FCSTD DOCUMENT  (FreeCAD 1.0R39109 (Git))
Label: Self Tap screw sketches V2
License: All rights reserved
LicenseURL: https://en.wikipedia.org/wiki/All_rights_reserved
objects: Sketcher::SketchObject×3
note: 6 computed .brp shape members not serialized (recipe doc carries the construction recipe); baked Part::Feature solids carry a one-line shape summary decoded from their .brp

FEATURE [Sketcher::SketchObject] Sketch  label="M3 self tap Sketch"
  ArcFitTolerance = 1e-06
  FullyConstrained = false
  MakeInternals = false
  MapMode = 5
  expr: Constraints[19] = .Constraints.Holeradius * 2 + 0.9 mm
  expr: Constraints[22] = .Constraints.Holeradius / 2
  sketch-geometry (10):
    g0: ArcOfCircle CenterX=-0.517439 CenterY=0.767765 CenterZ=0 NormalX=0 NormalY=0 NormalZ=1 AngleXU=0 Radius=1.6 StartAngle=0.890878 EndAngle=2.25072
    g1: ArcOfCircle CenterX=1.25791 CenterY=1.79277 CenterZ=0 NormalX=0 NormalY=0 NormalZ=1 AngleXU=0 Radius=0.8 StartAngle=2.86405 EndAngle=4.46634
    g2: ArcOfCircle CenterX=-0.517439 CenterY=0.767765 CenterZ=0 NormalX=0 NormalY=0 NormalZ=1 AngleXU=0 Radius=1.6 StartAngle=5.07967 EndAngle=6.43951
    g3: ArcOfCircle CenterX=-0.517439 CenterY=-1.28224 CenterZ=0 NormalX=0 NormalY=0 NormalZ=1 AngleXU=0 Radius=0.8 StartAngle=0.76965 EndAngle=2.37194
    g4: ArcOfCircle CenterX=-0.517439 CenterY=0.767765 CenterZ=0 NormalX=0 NormalY=0 NormalZ=1 AngleXU=0 Radius=1.6 StartAngle=2.98527 EndAngle=4.34511
    g5: ArcOfCircle CenterX=-2.29279 CenterY=1.79277 CenterZ=0 NormalX=0 NormalY=0 NormalZ=1 AngleXU=0 Radius=0.8 StartAngle=4.95844 EndAngle=6.56073
    g6: LineSegment [constr] StartX=1.25791 StartY=1.79277 StartZ=0 EndX=-2.29279 EndY=1.79277 EndZ=0
    g7: LineSegment [constr] StartX=-2.29279 StartY=1.79277 StartZ=0 EndX=-0.517439 EndY=-1.28224 EndZ=0
    g8: LineSegment [constr] StartX=-0.517439 StartY=-1.28224 StartZ=0 EndX=1.25791 EndY=1.79277 EndZ=0
    g9: Circle [constr] CenterX=-0.517439 CenterY=0.767765 CenterZ=0 NormalX=0 NormalY=0 NormalZ=1 AngleXU=0 Radius=2.05
  constraints (28):
    c: Coincident(g1,g0)
    c: Coincident(g2,g1)
    c: Coincident(g3,g2)
    c: Coincident(g4,g3)
    c: Coincident(g5,g4)
    c: Coincident(g5,g0)
    c: Equal(g0,g2)
    c: Equal(g2,g4)
    c: Coincident(g6,g7)
    c: Coincident(g7,g8)
    c: Coincident(g8,g6)
    c: Equal(g6,g7)
    c: Equal(g6,g8)
    c: PointOnObject(g6,g9)
    c: PointOnObject(g7,g9)
    c: PointOnObject(g8,g9)
    c: Coincident(g9,g0)
    c: Coincident(g8,g1)
    c: Radius(g0) = 1.6  'Holeradius'
    c: Diameter(g9) = 4.1
    c: Equal(g3,g1)
    c: Equal(g1,g5)
    c: Radius(g5) = 0.8
    c: Coincident(g0,g2)
    c: Coincident(g0,g4)
    c: Coincident(g6,g5)
    c: Coincident(g3,g7)
    c: Horizontal(g6)
FEATURE [Sketcher::SketchObject] Sketch001  label="M5 self tap Sketch"
  ArcFitTolerance = 1e-06
  FullyConstrained = false
  MakeInternals = false
  MapMode = 5
  expr: Constraints[19] = .Constraints.Holeradius * 2 + 0.9 mm
  expr: Constraints[22] = .Constraints.Holeradius / 2
  sketch-geometry (10):
    g0: ArcOfCircle CenterX=-0.363742 CenterY=0.173972 CenterZ=0 NormalX=0 NormalY=0 NormalZ=1 AngleXU=0 Radius=2.5 StartAngle=0.956395 EndAngle=2.1852
    g1: ArcOfCircle CenterX=2.19103 CenterY=1.64897 CenterZ=0 NormalX=0 NormalY=0 NormalZ=1 AngleXU=0 Radius=1.25 StartAngle=2.67008 EndAngle=4.66031
    g2: ArcOfCircle CenterX=-0.363742 CenterY=0.173972 CenterZ=0 NormalX=0 NormalY=0 NormalZ=1 AngleXU=0 Radius=2.5 StartAngle=5.14519 EndAngle=6.37399
    g3: ArcOfCircle CenterX=-0.363742 CenterY=-2.77603 CenterZ=0 NormalX=0 NormalY=0 NormalZ=1 AngleXU=0 Radius=1.25 StartAngle=0.575682 EndAngle=2.56591
    g4: ArcOfCircle CenterX=-0.363742 CenterY=0.173972 CenterZ=0 NormalX=0 NormalY=0 NormalZ=1 AngleXU=0 Radius=2.5 StartAngle=3.05079 EndAngle=4.27959
    g5: ArcOfCircle CenterX=-2.91852 CenterY=1.64897 CenterZ=0 NormalX=0 NormalY=0 NormalZ=1 AngleXU=0 Radius=1.25 StartAngle=4.76447 EndAngle=6.7547
    g6: LineSegment [constr] StartX=2.19103 StartY=1.64897 StartZ=0 EndX=-2.91852 EndY=1.64897 EndZ=0
    g7: LineSegment [constr] StartX=-2.91852 StartY=1.64897 StartZ=0 EndX=-0.363742 EndY=-2.77603 EndZ=0
    g8: LineSegment [constr] StartX=-0.363742 StartY=-2.77603 StartZ=0 EndX=2.19103 EndY=1.64897 EndZ=0
    g9: Circle [constr] CenterX=-0.363742 CenterY=0.173972 CenterZ=0 NormalX=0 NormalY=0 NormalZ=1 AngleXU=0 Radius=2.95
  constraints (28):
    c: Coincident(g1,g0)
    c: Coincident(g2,g1)
    c: Coincident(g3,g2)
    c: Coincident(g4,g3)
    c: Coincident(g5,g4)
    c: Coincident(g5,g0)
    c: Equal(g0,g2)
    c: Equal(g2,g4)
    c: Coincident(g6,g7)
    c: Coincident(g7,g8)
    c: Coincident(g8,g6)
    c: Equal(g6,g7)
    c: Equal(g6,g8)
    c: PointOnObject(g6,g9)
    c: PointOnObject(g7,g9)
    c: PointOnObject(g8,g9)
    c: Coincident(g9,g0)
    c: Coincident(g8,g1)
    c: Radius(g0) = 2.5  'Holeradius'
    c: Diameter(g9) = 5.9
    c: Equal(g3,g1)
    c: Equal(g1,g5)
    c: Radius(g5) = 1.25
    c: Coincident(g0,g2)
    c: Coincident(g0,g4)
    c: Coincident(g6,g5)
    c: Coincident(g3,g7)
    c: Horizontal(g6)
FEATURE [Sketcher::SketchObject] Sketch002  label="M4 self tap Sketch"
  ArcFitTolerance = 1e-06
  FullyConstrained = false
  MakeInternals = false
  MapMode = 5
  expr: Constraints[19] = .Constraints.Holeradius * 2 + 0.9 mm
  expr: Constraints[22] = .Constraints.Holeradius / 2
  sketch-geometry (10):
    g0: ArcOfCircle CenterX=-0.414672 CenterY=0.379342 CenterZ=0 NormalX=0 NormalY=0 NormalZ=1 AngleXU=0 Radius=2 StartAngle=0.929815 EndAngle=2.21178
    g1: ArcOfCircle CenterX=1.70709 CenterY=1.60434 CenterZ=0 NormalX=0 NormalY=0 NormalZ=1 AngleXU=0 Radius=1 StartAngle=2.75394 EndAngle=4.57645
    g2: ArcOfCircle CenterX=-0.414672 CenterY=0.379342 CenterZ=0 NormalX=0 NormalY=0 NormalZ=1 AngleXU=0 Radius=2 StartAngle=5.11861 EndAngle=6.40057
    g3: ArcOfCircle CenterX=-0.414672 CenterY=-2.07066 CenterZ=0 NormalX=0 NormalY=0 NormalZ=1 AngleXU=0 Radius=1 StartAngle=0.659542 EndAngle=2.48205
    g4: ArcOfCircle CenterX=-0.414672 CenterY=0.379342 CenterZ=0 NormalX=0 NormalY=0 NormalZ=1 AngleXU=0 Radius=2 StartAngle=3.02421 EndAngle=4.30617
    g5: ArcOfCircle CenterX=-2.53643 CenterY=1.60434 CenterZ=0 NormalX=0 NormalY=0 NormalZ=1 AngleXU=0 Radius=1 StartAngle=4.84833 EndAngle=6.67084
    g6: LineSegment [constr] StartX=1.70709 StartY=1.60434 StartZ=0 EndX=-2.53643 EndY=1.60434 EndZ=0
    g7: LineSegment [constr] StartX=-2.53643 StartY=1.60434 StartZ=0 EndX=-0.414672 EndY=-2.07066 EndZ=0
    g8: LineSegment [constr] StartX=-0.414672 StartY=-2.07066 StartZ=0 EndX=1.70709 EndY=1.60434 EndZ=0
    g9: Circle [constr] CenterX=-0.414672 CenterY=0.379342 CenterZ=0 NormalX=0 NormalY=0 NormalZ=1 AngleXU=0 Radius=2.45
  constraints (28):
    c: Coincident(g1,g0)
    c: Coincident(g2,g1)
    c: Coincident(g3,g2)
    c: Coincident(g4,g3)
    c: Coincident(g5,g4)
    c: Coincident(g5,g0)
    c: Equal(g0,g2)
    c: Equal(g2,g4)
    c: Coincident(g6,g7)
    c: Coincident(g7,g8)
    c: Coincident(g8,g6)
    c: Equal(g6,g7)
    c: Equal(g6,g8)
    c: PointOnObject(g6,g9)
    c: PointOnObject(g7,g9)
    c: PointOnObject(g8,g9)
    c: Coincident(g9,g0)
    c: Coincident(g8,g1)
    c: Radius(g0) = 2  'Holeradius'
    c: Diameter(g9) = 4.9
    c: Equal(g3,g1)
    c: Equal(g1,g5)
    c: Radius(g5) = 1
    c: Coincident(g0,g2)
    c: Coincident(g0,g4)
    c: Coincident(g6,g5)
    c: Coincident(g3,g7)
    c: Horizontal(g6)
